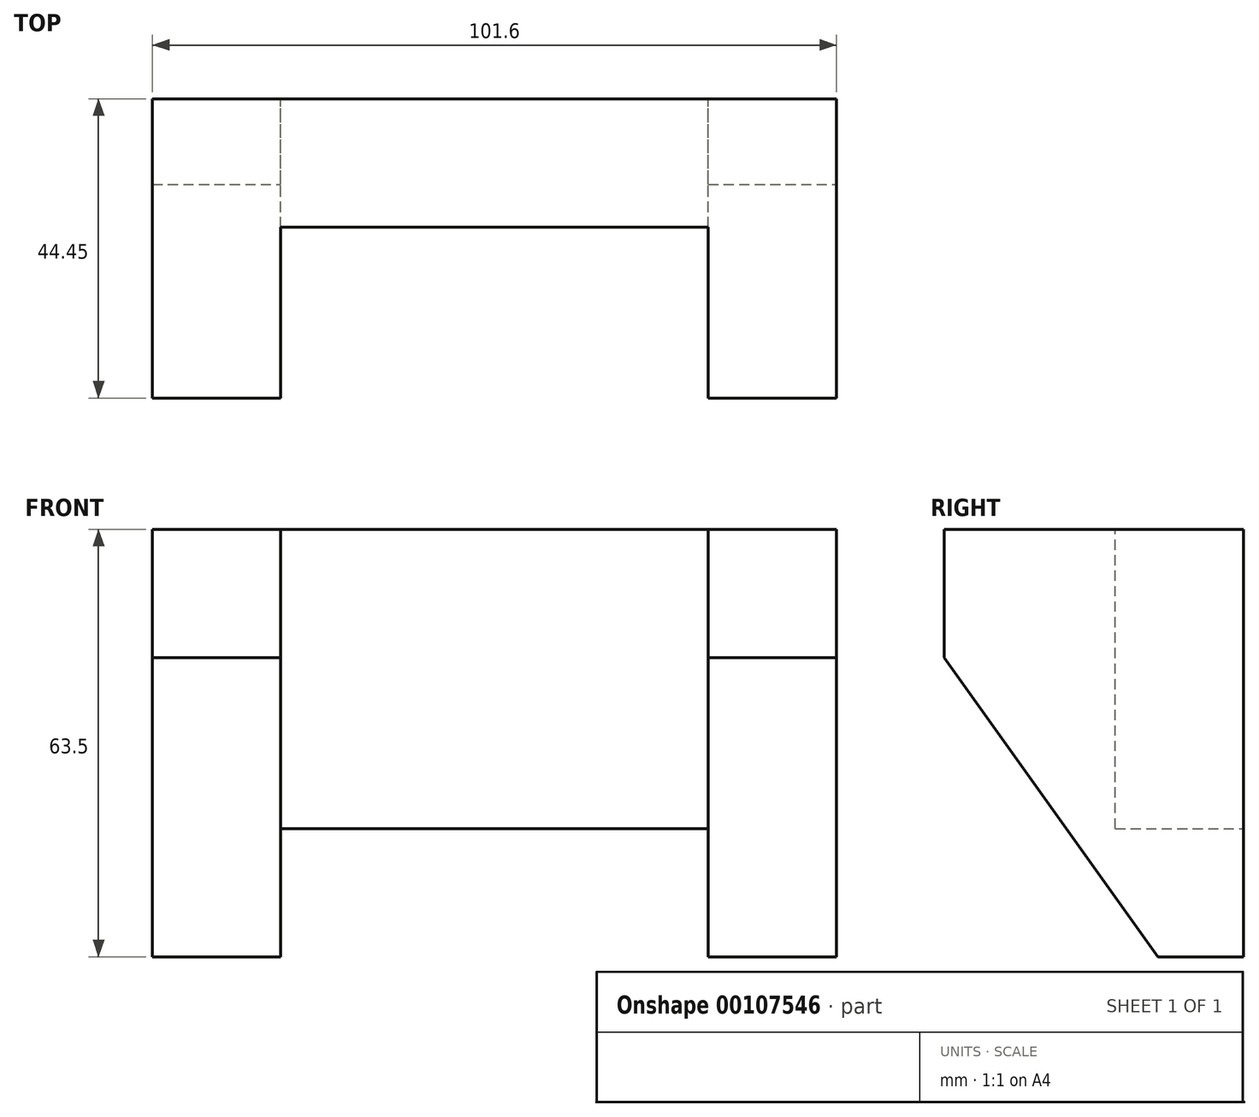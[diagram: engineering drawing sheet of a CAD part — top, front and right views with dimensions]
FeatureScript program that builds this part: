
annotation { "Feature Type Name" : "Feature", "Feature Type Description" : "" }
export const myFeature = defineFeature(function(context is Context, id is Id, definition is map)
    precondition{}
    {
        {
            var Q0;
            Q0=qCreatedBy(makeId("Front.planeOp"),FACE);
            var sketch = newSketch(context, id + "F0", { "sketchPlane" : qUnion([Q0])});
            skLineSegment(sketch, "E0", {"start": v(-46.92, -40.46) * mm, "end": v(-27.87, -40.46) * mm});
            skLineSegment(sketch, "E1", {"start": v(-27.87, -40.46) * mm, "end": v(-27.87, -21.4) * mm});
            skLineSegment(sketch, "E2", {"start": v(-27.87, -21.4) * mm, "end": v(35.63, -21.4) * mm});
            skLineSegment(sketch, "E3", {"start": v(35.63, -21.4) * mm, "end": v(35.63, -40.46) * mm});
            skLineSegment(sketch, "E4", {"start": v(35.63, -40.46) * mm, "end": v(54.68, -40.46) * mm});
            skLineSegment(sketch, "E5", {"start": v(54.68, -40.46) * mm, "end": v(54.68, 23.04) * mm});
            skLineSegment(sketch, "E6", {"start": v(54.68, 23.04) * mm, "end": v(-46.92, 23.04) * mm});
            skLineSegment(sketch, "E7", {"start": v(-46.92, 23.04) * mm, "end": v(-46.92, -40.46) * mm});
            skLineSegment(sketch, "E8", {"start": v(-27.87, -21.4) * mm, "end": v(-27.87, 23.04) * mm});
            skLineSegment(sketch, "E9", {"start": v(35.63, -21.4) * mm, "end": v(35.63, 23.04) * mm});
            skSolve(sketch);
        }
        {
            var Q0;
            Q0=makeQuery(id+"F0.imprint","IMPRINT",FACE,{"disambiguationData":[TD([[makeQuery(id+"F0.imprint","IMPRINT",EDGE,{"derivedFrom":sQuery(id+"F0.wireOp",EDGE,"E2")}),1.0]])]});
            extrude(context, id + "F1", {"entities" : qUnion([Q0]), "depth" : 19.05 * mm});
        }
        {
            var Q0;
            Q0=makeQuery(id+"F0.imprint","IMPRINT",FACE,{"disambiguationData":[TD([[makeQuery(id+"F0.imprint","IMPRINT",EDGE,{"derivedFrom":sQuery(id+"F0.wireOp",EDGE,"E3")}),1.0]])]});
            var Q1;
            Q1=makeQuery(id+"F0.imprint","IMPRINT",FACE,{"disambiguationData":[TD([[makeQuery(id+"F0.imprint","IMPRINT",EDGE,{"derivedFrom":sQuery(id+"F0.wireOp",EDGE,"E0")}),1.0]])]});
            extrude(context, id + "F2", {"entities" : qUnion([Q0, Q1]), "operationType" : NewBodyOperationType.ADD, "depth" : 44.45 * mm});
        }
        {
            var Q0;
            Q0=makeQuery(id+"F2.opExtrude","SWEPT_FACE",FACE,{"disambiguationData":[OSD([sQuery(id+"F0.wireOp",EDGE,"E5")])]});
            var sketch = newSketch(context, id + "F3", { "sketchPlane" : qUnion([Q0])});
            skLineSegment(sketch, "E10", {"start": v(0, 23.04) * mm, "end": v(-44.45, 23.04) * mm});
            skLineSegment(sketch, "E11", {"start": v(-44.45, 23.04) * mm, "end": v(-44.45, 4) * mm});
            skLineSegment(sketch, "E12", {"start": v(-44.45, 4) * mm, "end": v(-44.45, -40.46) * mm});
            skLineSegment(sketch, "E13", {"start": v(-44.45, -40.46) * mm, "end": v(0, -40.46) * mm});
            skLineSegment(sketch, "E14", {"start": v(0, -40.46) * mm, "end": v(0, 23.04) * mm});
            skLineSegment(sketch, "E15", {"start": v(-12.7, -40.46) * mm, "end": v(0, -40.46) * mm});
            skLineSegment(sketch, "E16", {"start": v(-12.7, -40.46) * mm, "end": v(-44.45, 4) * mm});
            skSolve(sketch);
        }
        {
            var Q0;
            Q0=makeQuery(id+"F3.imprint","IMPRINT",FACE,{"disambiguationData":[TD([[makeQuery(id+"F3.imprint","IMPRINT",EDGE,{"derivedFrom":sQuery(id+"F3.wireOp",EDGE,"E12")}),-1.0]])]});
            extrude(context, id + "F4", {"entities" : qUnion([Q0]), "operationType" : NewBodyOperationType.REMOVE, "endBound" : BoundingType.THROUGH_ALL, "oppositeDirection" : true, "depth" : 25.4 * mm});
        }
    });
